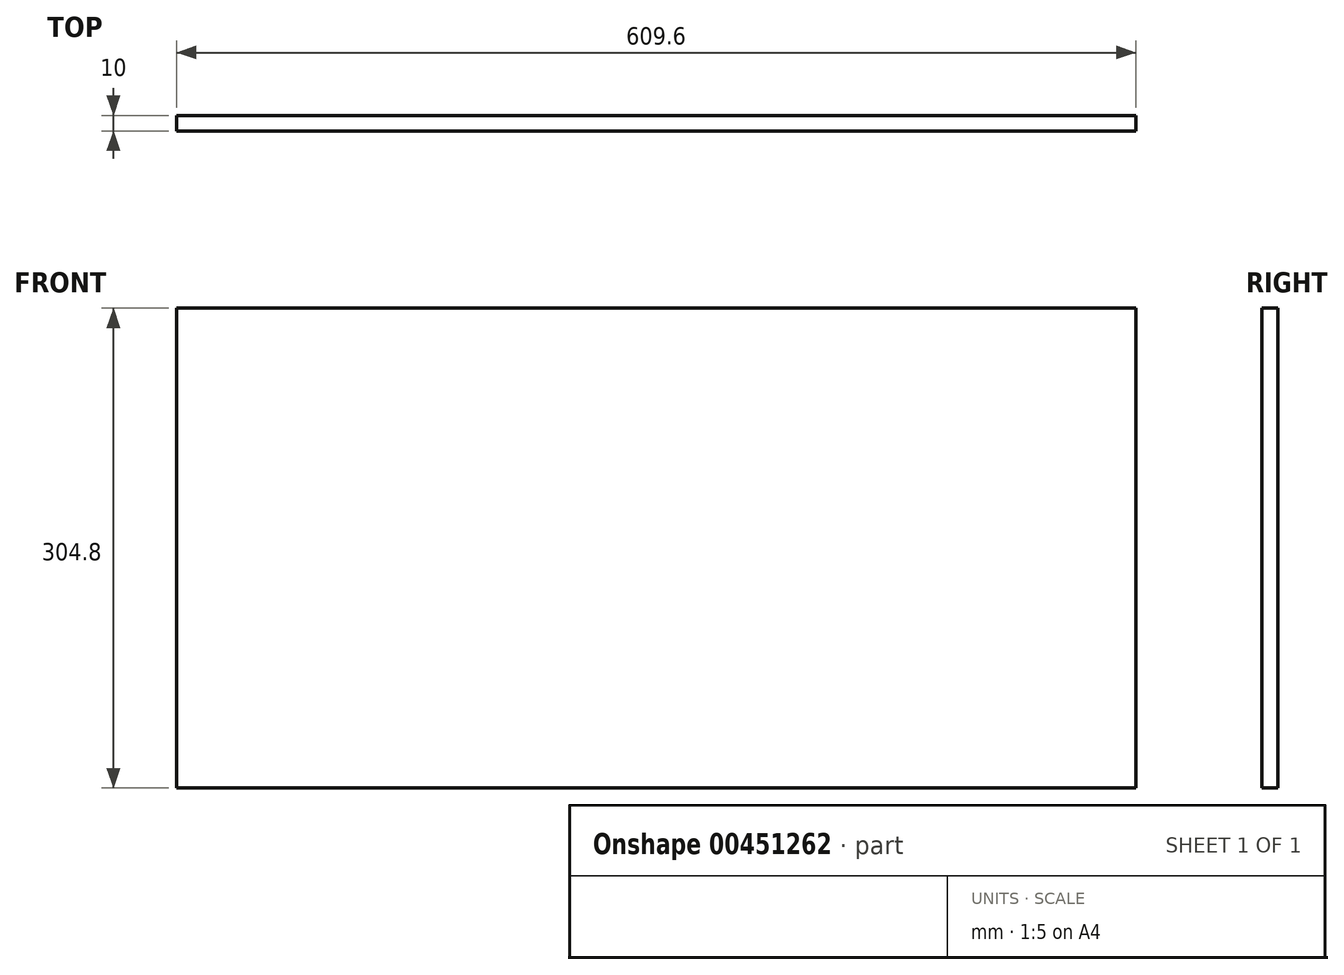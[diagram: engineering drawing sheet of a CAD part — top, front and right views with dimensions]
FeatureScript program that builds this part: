
annotation { "Feature Type Name" : "Feature", "Feature Type Description" : "" }
export const myFeature = defineFeature(function(context is Context, id is Id, definition is map)
    precondition{}
    {
        {
            var Q0;
            Q0=qCreatedBy(makeId("Front.planeOp"),FACE);
            var sketch = newSketch(context, id + "F0", { "sketchPlane" : qUnion([Q0])});
            skLineSegment(sketch, "E0.bottom", {"start": v(304.8, -152.4) * mm, "end": v(-304.8, -152.4) * mm});
            skLineSegment(sketch, "E0.top", {"start": v(304.8, 152.4) * mm, "end": v(-304.8, 152.4) * mm});
            skLineSegment(sketch, "E0.left", {"start": v(304.8, -152.4) * mm, "end": v(304.8, 152.4) * mm});
            skLineSegment(sketch, "E0.right", {"start": v(-304.8, -152.4) * mm, "end": v(-304.8, 152.4) * mm});
            skPoint(sketch, "E0.middle", {"position": v(0, 0) * mm});
            skSolve(sketch);
        }
        {
            var Q0;
            Q0=makeQuery(id+"F0.imprint","IMPRINT",FACE,{"disambiguationData":[TD([[makeQuery(id+"F0.imprint","IMPRINT",EDGE,{"derivedFrom":sQuery(id+"F0.wireOp",EDGE,"E0.bottom")}),-1.0]])]});
            extrude(context, id + "F1", {"entities" : qUnion([Q0]), "depth" : 10 * mm});
        }
    });
